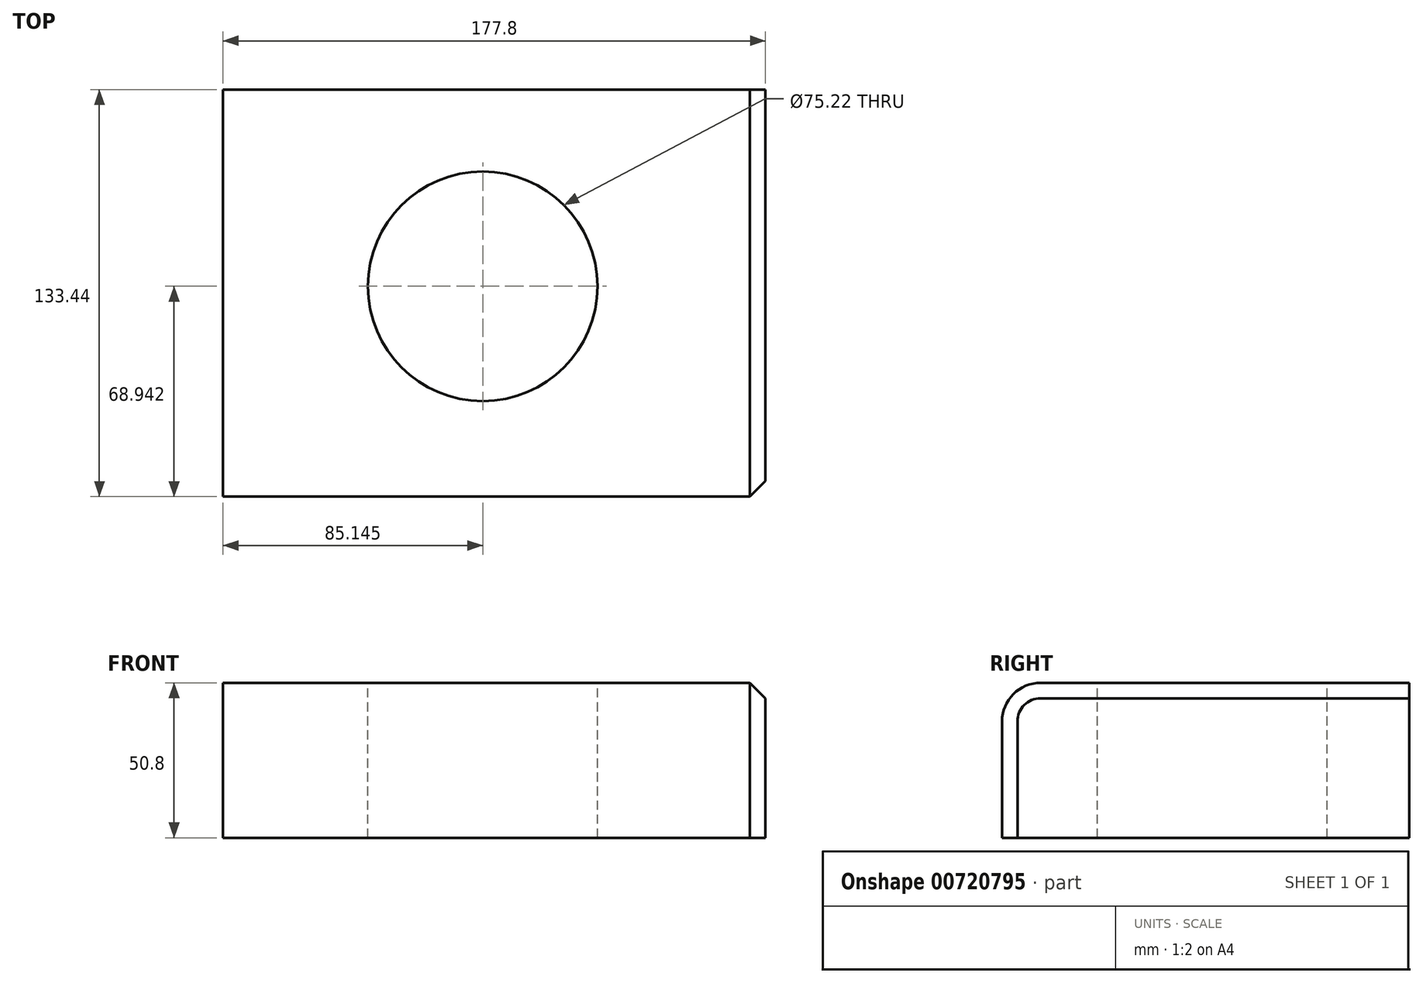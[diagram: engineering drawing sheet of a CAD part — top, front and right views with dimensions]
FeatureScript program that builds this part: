
annotation { "Feature Type Name" : "Feature", "Feature Type Description" : "" }
export const myFeature = defineFeature(function(context is Context, id is Id, definition is map)
    precondition{}
    {
        {
            var Q0;
            Q0=qCreatedBy(makeId("Top.planeOp"),FACE);
            var sketch = newSketch(context, id + "F0", { "sketchPlane" : qUnion([Q0])});
            skLineSegment(sketch, "E0.bottom", {"start": v(0, 0) * mm, "end": v(177.8, 0) * mm});
            skLineSegment(sketch, "E0.top", {"start": v(0, -133.44) * mm, "end": v(177.8, -133.44) * mm});
            skLineSegment(sketch, "E0.left", {"start": v(0, 0) * mm, "end": v(0, -133.44) * mm});
            skLineSegment(sketch, "E0.right", {"start": v(177.8, 0) * mm, "end": v(177.8, -133.44) * mm});
            skPoint(sketch, "E1.firstSnap0", {"position": v(177.8, -66.72) * mm});
            skLineSegment(sketch, "E1.bottom", {"start": v(40.52, -66.72) * mm, "end": v(150.04, -66.72) * mm});
            skLineSegment(sketch, "E1.top", {"start": v(40.52, -133.44) * mm, "end": v(150.04, -133.44) * mm});
            skLineSegment(sketch, "E1.left", {"start": v(40.52, -66.72) * mm, "end": v(40.52, -133.44) * mm});
            skLineSegment(sketch, "E1.right", {"start": v(150.04, -66.72) * mm, "end": v(150.04, -133.44) * mm});
            skSolve(sketch);
        }
        {
            var Q0;
            Q0=makeQuery(id+"F0.imprint","IMPRINT",FACE,{"disambiguationData":[TD([[makeQuery(id+"F0.imprint","IMPRINT",EDGE,{"derivedFrom":sQuery(id+"F0.wireOp",EDGE,"E0.bottom")}),-1.0]])]});
            var Q1;
            Q1=makeQuery(id+"F0.imprint","IMPRINT",FACE,{"disambiguationData":[TD([[makeQuery(id+"F0.imprint","IMPRINT",EDGE,{"derivedFrom":sQuery(id+"F0.wireOp",EDGE,"E1.bottom")}),-1.0]])]});
            extrude(context, id + "F1", {"entities" : qUnion([Q0, Q1]), "depth" : 50.8 * mm, "offsetDistance" : 25.4 * mm});
        }
        {
            var Q0;
            Q0=makeQuery(id+"F1.opExtrude","CAP_FACE",FACE,{"disambiguationData":[OSD([sQuery(id+"F0.wireOp",EDGE,"E0.bottom"),sQuery(id+"F0.wireOp",EDGE,"E0.top"),sQuery(id+"F0.wireOp",EDGE,"E0.left"),sQuery(id+"F0.wireOp",EDGE,"E0.right"),sQuery(id+"F0.wireOp",EDGE,"E1.top")])],"isStart":false});
            var sketch = newSketch(context, id + "F2", { "sketchPlane" : qUnion([Q0])});
            skCircle(sketch, "E2", {"center": v(85.14, -64.5) * mm, "radius": 37.61 * mm});
            skSolve(sketch);
        }
        {
            var Q0;
            Q0=makeQuery(id+"F2.imprint","IMPRINT",FACE,{"disambiguationData":[TD([[makeQuery(id+"F2.imprint","IMPRINT",EDGE,{"derivedFrom":sQuery(id+"F2.wireOp",EDGE,"E2")}),1.0]])]});
            extrude(context, id + "F3", {"entities" : qUnion([Q0]), "operationType" : NewBodyOperationType.REMOVE, "endBound" : BoundingType.THROUGH_ALL, "oppositeDirection" : true, "depth" : 25.4 * mm, "offsetDistance" : 25.4 * mm});
        }
        {
            var Q0;
            Q0=makeQuery(id+"F1.opExtrude","CAP_EDGE",EDGE,{"disambiguationData":[OSD([sQuery(id+"F0.wireOp",EDGE,"E0.top"),sQuery(id+"F0.wireOp",EDGE,"E1.top")])],"isStart":false});
            fillet(context, id + "F4", {"entities" : qUnion([Q0]), "radius" : 12.7 * mm, "tangentPropagation" : true, "allowEdgeOverflow" : false});
        }
        {
            var Q0;
            Q0=makeQuery(id+"F1.opExtrude","CAP_EDGE",EDGE,{"disambiguationData":[OSD([sQuery(id+"F0.wireOp",EDGE,"E0.right")])],"isStart":false});
            chamfer(context, id + "F5", {"entities" : qUnion([Q0]), "width" : 5.08 * mm, "tangentPropagation" : true});
        }
    });
